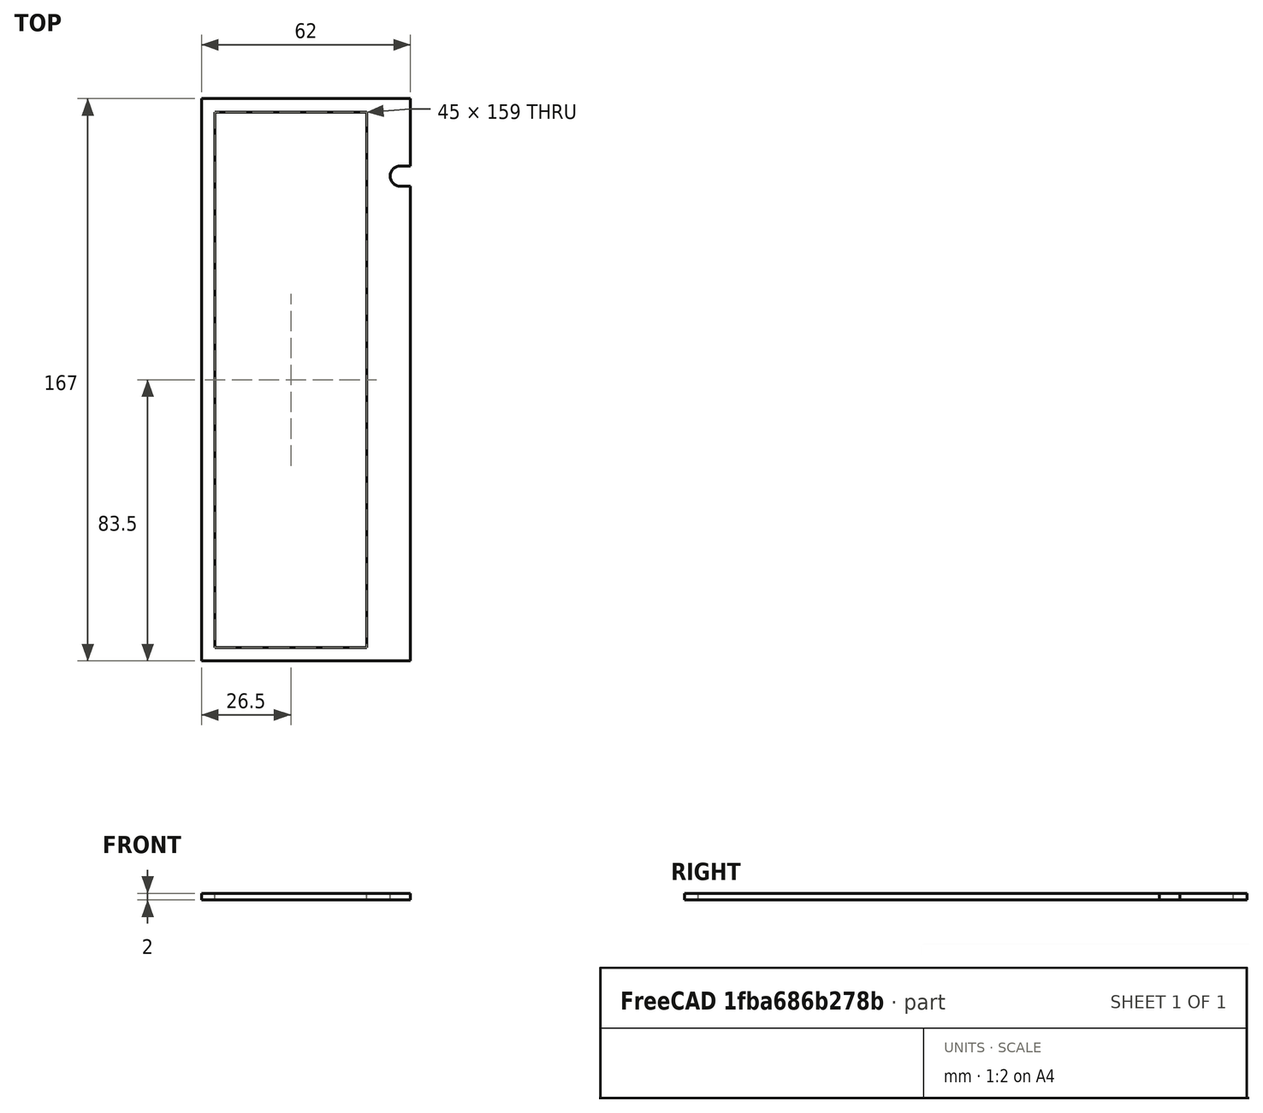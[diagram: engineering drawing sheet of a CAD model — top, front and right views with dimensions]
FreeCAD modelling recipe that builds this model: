
FCSTD DOCUMENT  (FreeCAD 0.16R6703 (Git))
Label: Carátula Conectores
License: All rights reserved
LicenseURL: http://en.wikipedia.org/wiki/All_rights_reserved
objects: Part::Box×3, Part::Cut×2, Part::Cylinder×1, Part::MultiFuse×1
note: 7 computed .brp shape members not serialized (recipe doc carries the construction recipe); baked Part::Feature solids carry a one-line shape summary decoded from their .brp

FEATURE [Part::Box] Box  label="Cube"
  Height = 3
  Length = 45
  Width = 159
FEATURE [Part::Box] Box001  label="Cube001"
  Height = 2
  Length = 62
  Placement = pos=(-4,-4,0) rot=(0,0,1;0rad)
  Width = 167
FEATURE [Part::Cylinder] Cylinder
  Angle = 360
  Height = 10
  Placement = pos=(55,140,0) rot=(0,0,1;0rad)
  Radius = 3
FEATURE [Part::MultiFuse] Fusion
  Shapes = -> [Cylinder,Box]
FEATURE [Part::Cut] Cut
  Base = -> Box001
  Tool = -> Fusion
FEATURE [Part::Box] Box002  label="Cube002"
  Height = 10
  Length = 6
  Placement = pos=(55,137,0) rot=(0,0,1;0rad)
  Width = 6
FEATURE [Part::Cut] Cut001
  Base = -> Cut
  Tool = -> Box002
